# Revit family: Door_Swing_Dunbarton_RediFrame
name_source: partatom
category: Doors
units: mm (PartAtom-declared; Revit-internal decimal feet)

## family parameters
Always vertical = Yes
Cut with Voids When Loaded = No
Host = Wall
OmniClass Number = 23.30.10.17.17
OmniClass Title = Folding Doors and Grilles
Room Calculation Point = No
Shared = No

## types (4) — shared parameters
Air Infiltration = as Specified
Assembly Code = C1020100
Door Panel Type = as Specified
Door Thickness = 0' - 1"
Fire Rating = 90 Minute Neutral and Positive Pressure  ;  Wood or Steel
Frame Thickness = 0' - 0 5/8"
Function = Interior
Green Building-LEED = http://www.arcat.com
Impact Resistance = as Specified
Installation-Fabrication = https://dunbarton.com
Keynote = 08 11 10
Manufacturer = Dunbarton Corporation
Manufacturer Fax = 334-793-7022
Manufacturer Website = https://dunbarton.com
Opening Height = 6' - 8"
Product Data = http://www.arcat.com
Product Properties = https://dunbarton.com
RO Spacing Sides = 0' - 0 1/4"
RO Spacing Top = 0' - 0 1/4"
Rough Height = 0' - 0"
Rough Width = 0' - 0"
Sales Information = https://dunbarton.com
Specification = http://www.arcat.com
Standards Conformance = Level A Durability ANSI 250.5-1994
Structural Test Pressure = as Specified
Thickness = 0' - 0"
URL = https://dunbarton.com
Unit Width = 3' - 0"
Wall Closure = By host
Water Penetration = as Specified
Width = 3' - 0"
zero-valued in all types: Expected Lifespan (Years), Maintenance Schedule (Months), R-Value, Warranty Duration (Years)

## per-type parameters (varying)
| type | Description | Frame Type | Model | Type Comments |
| 134 Kerf Frame | Dunbarton Steel Swing Door Frame - RediFrame Kerf as Specified | RediFrame134Kerf | RediFrame 134 Kerf | Wall Depths as Specified |
| 134-138 Frame | Dunbarton Steel Swing Door Frame - RediFrame as Specified | RediFrame134138 | RediFrame 134-138 | Available Wall Depths : 4 , 4.5 , 4.625 , 4.75 , 4.875 , 5.25 , 5.375 , 6.75 , 6.875 , 7.375 |
| 138 Frame | Dunbarton Steel Swing Door Frame - RediFrame as Specified | RediFrame138 | RediFrame 138 | Available Wall Depths : 2.625 , 2.875 , 3.5 , 3.625 , 3.75 |
| 134 Frame | Dunbarton Steel Swing Door Frame - RediFrame as Specified | RediFrame134 | RediFrame 134 | Available Wall Depths : 2.875 , 3.5 , 3.625 , 3.75 |

## geometry (parser evidence)
native form markers: Sweep x27
no freeform markers — native parametric forms only
